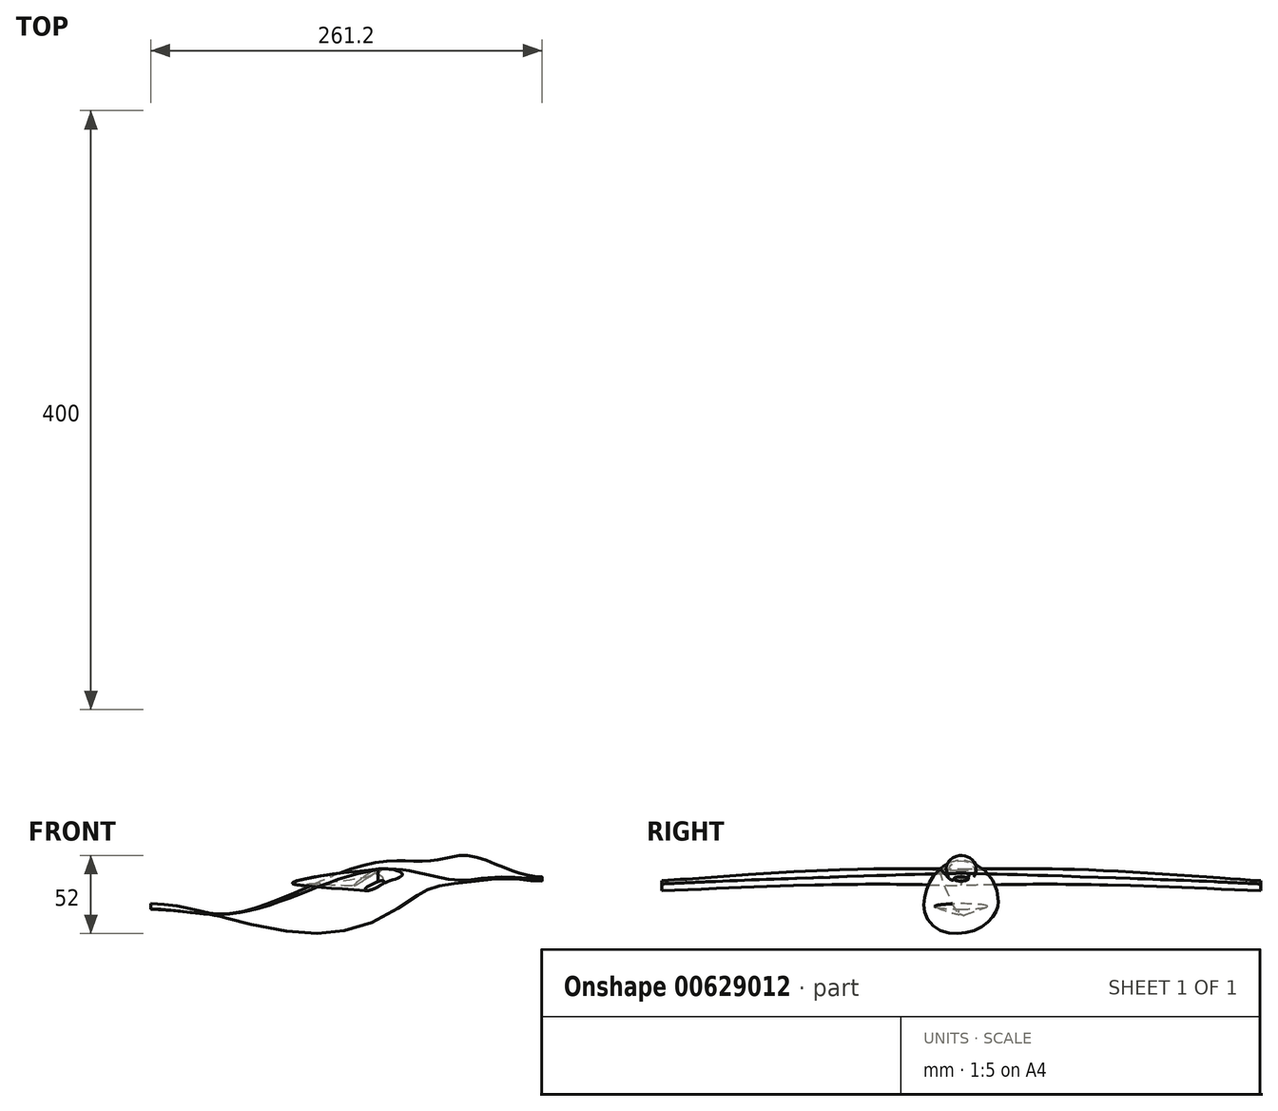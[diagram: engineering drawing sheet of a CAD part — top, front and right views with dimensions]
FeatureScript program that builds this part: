
annotation { "Feature Type Name" : "Feature", "Feature Type Description" : "" }
export const myFeature = defineFeature(function(context is Context, id is Id, definition is map)
    precondition{}
    {
        {
            var Q0;
            Q0=qCreatedBy(makeId("Front.planeOp"),FACE);
            var sketch = newSketch(context, id + "F0", { "sketchPlane" : qUnion([Q0])});
            skFitSpline(sketch, "E0", {"points": [v(-84.41, 5.07) * mm, v(-53.05, 3.5) * mm, v(-25.7, 11.37) * mm, v(6.23, 29.99) * mm, v(29, 38.44) * mm, v(45.9, 41.59) * mm, v(67.8, 40.44) * mm, v(80.55, 33.71) * mm, v(96.01, 29.7) * mm], "startDerivative": vector(310.96, -44.42) * mm, "endDerivative": vector(203.12, -4.15) * mm});
            skSolve(sketch);
        }
        {
            var Q0;
            Q0=qCreatedBy(makeId("Right.planeOp"),FACE);
            cPlane(context, id + "F1", {"entities" : qUnion([Q0]), "cplaneType" : CPlaneType.OFFSET, "offset" : 96 * mm, "width" : 150 * mm, "height" : 150 * mm});
        }
        {
            var Q0;
            Q0=qCreatedBy(makeId("Right.planeOp"),FACE);
            cPlane(context, id + "F2", {"entities" : qUnion([Q0]), "cplaneType" : CPlaneType.OFFSET, "offset" : 116.2 * mm, "oppositeDirection" : true, "width" : 150 * mm, "height" : 150 * mm});
        }
        {
            var Q0;
            Q0=qCreatedBy(id+"F2.planeOp",FACE);
            var sketch = newSketch(context, id + "F3", { "sketchPlane" : qUnion([Q0])});
            skEllipse(sketch, "E1", {"center": v(0, 5.07) * mm, "majorRadius": 2.78 * mm, "minorRadius": 1.24 * mm, "majorAxis": v(1, 0)});
            skSolve(sketch);
        }
        {
            var Q0;
            Q0=qCreatedBy(id+"F1.planeOp",FACE);
            var sketch = newSketch(context, id + "F4", { "sketchPlane" : qUnion([Q0])});
            skEllipse(sketch, "E2", {"center": v(0, 29.7) * mm, "majorRadius": 5 * mm, "minorRadius": 1.42 * mm, "majorAxis": v(-1, 0)});
            skSolve(sketch);
        }
        {
            var Q0;
            Q0=qCreatedBy(makeId("Right.planeOp"),FACE);
            var sketch = newSketch(context, id + "F5", { "sketchPlane" : qUnion([Q0])});
            skEllipse(sketch, "E3", {"center": v(0, 25.98) * mm, "majorRadius": 17.61 * mm, "minorRadius": 16 * mm, "majorAxis": v(-1, 0)});
            skSolve(sketch);
        }
        {
            var Q0;
            Q0=qCreatedBy(makeId("Right.planeOp"),FACE);
            cPlane(context, id + "F6", {"entities" : qUnion([Q0]), "cplaneType" : CPlaneType.OFFSET, "offset" : 45 * mm, "width" : 150 * mm, "height" : 150 * mm});
        }
        {
            var Q0;
            Q0=qCreatedBy(id+"F6.planeOp",FACE);
            var sketch = newSketch(context, id + "F7", { "sketchPlane" : qUnion([Q0])});
            skEllipse(sketch, "E4", {"center": v(0, 36.3) * mm, "majorRadius": 10 * mm, "minorRadius": 9 * mm, "majorAxis": v(-1, 0)});
            skSolve(sketch);
        }
        {
            var Q0;
            Q0=qCreatedBy(id+"F6.planeOp",FACE);
            cPlane(context, id + "F8", {"entities" : qUnion([Q0]), "cplaneType" : CPlaneType.OFFSET, "offset" : 17.1 * mm, "width" : 150 * mm, "height" : 150 * mm});
        }
        {
            var Q0;
            Q0=qCreatedBy(id+"F8.planeOp",FACE);
            var sketch = newSketch(context, id + "F9", { "sketchPlane" : qUnion([Q0])});
            skEllipse(sketch, "E5", {"center": v(0, 35.27) * mm, "majorRadius": 7.9 * mm, "minorRadius": 5.53 * mm, "majorAxis": v(-1, 0)});
            skSolve(sketch);
        }
        {
            var Q0;
            Q0=qCreatedBy(id+"F2.planeOp",FACE);
            cPlane(context, id + "F10", {"entities" : qUnion([Q0]), "cplaneType" : CPlaneType.OFFSET, "offset" : 49 * mm, "oppositeDirection" : true, "width" : 150 * mm, "height" : 150 * mm});
        }
        {
            var Q0;
            Q0=qCreatedBy(id+"F10.planeOp",FACE);
            var sketch = newSketch(context, id + "F11", { "sketchPlane" : qUnion([Q0])});
            skEllipse(sketch, "E6", {"center": v(0, 11.37) * mm, "majorRadius": 17.57 * mm, "minorRadius": 1.8 * mm, "majorAxis": v(-1, 0)});
            skSolve(sketch);
        }
        {
            var Q0;
            Q0=makeQuery(id+"F4.imprint","IMPRINT",FACE,{"disambiguationData":[TD([[makeQuery(id+"F4.imprint","IMPRINT",EDGE,{"derivedFrom":sQuery(id+"F4.wireOp",EDGE,"E2")}),1.0]])]});
            var Q1;
            Q1=makeQuery(id+"F9.imprint","IMPRINT",FACE,{"disambiguationData":[TD([[makeQuery(id+"F9.imprint","IMPRINT",EDGE,{"derivedFrom":sQuery(id+"F9.wireOp",EDGE,"E5")}),1.0]])]});
            var Q2;
            Q2=makeQuery(id+"F7.imprint","IMPRINT",FACE,{"disambiguationData":[TD([[makeQuery(id+"F7.imprint","IMPRINT",EDGE,{"derivedFrom":sQuery(id+"F7.wireOp",EDGE,"E4")}),1.0]])]});
            var Q3;
            Q3=makeQuery(id+"F5.imprint","IMPRINT",FACE,{"disambiguationData":[TD([[makeQuery(id+"F5.imprint","IMPRINT",EDGE,{"derivedFrom":sQuery(id+"F5.wireOp",EDGE,"E3")}),1.0]])]});
            var Q4;
            Q4=makeQuery(id+"F3.imprint","IMPRINT",FACE,{"disambiguationData":[TD([[makeQuery(id+"F3.imprint","IMPRINT",EDGE,{"derivedFrom":sQuery(id+"F3.wireOp",EDGE,"E1")}),1.0]])]});
            var Q5;
            Q5=makeQuery(id+"F11.imprint","IMPRINT",FACE,{"disambiguationData":[TD([[makeQuery(id+"F11.imprint","IMPRINT",EDGE,{"derivedFrom":sQuery(id+"F11.wireOp",EDGE,"E6")}),1.0]])]});
            loft(context, id + "F12", {"startCondition" : LoftEndDerivativeType.NORMAL_TO_PROFILE, "startMagnitude" : 1, "endCondition" : LoftEndDerivativeType.NORMAL_TO_PROFILE, "endMagnitude" : 1, "sheetProfilesArray" : [{ "sheetProfileEntities" : qUnion([Q0]) }, { "sheetProfileEntities" : qUnion([Q1]) }, { "sheetProfileEntities" : qUnion([Q2]) }, { "sheetProfileEntities" : qUnion([Q3]) }, { "sheetProfileEntities" : qUnion([Q4]) }, { "sheetProfileEntities" : qUnion([Q5]) }]});
        }
        {
            var Q0;
            Q0=qCreatedBy(makeId("Front.planeOp"),FACE);
            var sketch = newSketch(context, id + "F13", { "sketchPlane" : qUnion([Q0])});
            skLineSegment(sketch, "E7", {"start": v(-58.76, 13.59) * mm, "end": v(0, 35.7) * mm});
            skSolve(sketch);
        }
        {
            var Q0;
            Q0=qCreatedBy(makeId("Front.planeOp"),FACE);
            cPlane(context, id + "F14", {"entities" : qUnion([Q0]), "cplaneType" : CPlaneType.OFFSET, "offset" : 200 * mm, "width" : 150 * mm, "height" : 150 * mm});
        }
        {
            var Q0;
            Q0=qCreatedBy(makeId("Front.planeOp"),FACE);
            cPlane(context, id + "F15", {"entities" : qUnion([Q0]), "cplaneType" : CPlaneType.OFFSET, "offset" : 49 * mm, "width" : 150 * mm, "height" : 150 * mm});
        }
        {
            var Q0;
            Q0=qCreatedBy(makeId("Front.planeOp"),FACE);
            var sketch = newSketch(context, id + "F16", { "sketchPlane" : qUnion([Q0])});
            skEllipticalArc(sketch, "E8", {});
            skEllipticalArc(sketch, "E9", {});
            const initialGuessF16  = {"E8": [-0.017298103401628084, 0.03379535302519832, -0.8237704339825465, -0.566923515208374, 0.015067684936084414, 0.0010891221126240588, 4.662685079881785, 1.6451477373924313], "E9": [-0.014588911086320877, 0.03496590629220011, 0.9849873090560092, 0.17262676790869394, 0.0029575265624903397, 0.001370500930630289, 4.218962995655077, 2.6759421118494005]};
            skSetInitialGuess(sketch, initialGuessF16);
            skSolve(sketch);
        }
        {
            var Q0;
            Q0=qCreatedBy(id+"F15.planeOp",FACE);
            var sketch = newSketch(context, id + "F17", { "sketchPlane" : qUnion([Q0])});
            skEllipticalArc(sketch, "E10", {});
            skEllipticalArc(sketch, "E11", {});
            const initialGuessF17  = {"E10": [-0.032589975744485855, 0.0313419997692108, -0.9890317433706793, -0.14770311644292416, 0.030822984306227378, 0.0024839906210862156, 4.077982171427082, 2.2809984880084127], "E11": [-0.00894947163760662, 0.03431832045316696, 0.9996639704356599, -0.02592192533005802, 0.008555501838095957, 0.0021409207846646914, 4.29899924266966, 2.3333235677117328]};
            skSetInitialGuess(sketch, initialGuessF17);
            skSolve(sketch);
        }
        {
            var Q0;
            Q0=qCreatedBy(id+"F14.planeOp",FACE);
            var sketch = newSketch(context, id + "F18", { "sketchPlane" : qUnion([Q0])});
            skEllipticalArc(sketch, "E12", {});
            skEllipticalArc(sketch, "E13", {});
            const initialGuessF18  = {"E12": [-0.016077956184744835, 0.024971546605229378, -0.9096880175977404, -0.4152923195040971, 0.0069856411031233275, 0.0016369145110534853, 4.230009728268898, 2.495065859207771], "E13": [-0.01159256137907505, 0.0273281279951334, 0.9853504377429596, 0.1705418272441046, 0.002518639731580008, 0.0011575756907042255, 5.04476189844623, 2.525653687221013]};
            skSetInitialGuess(sketch, initialGuessF18);
            skSolve(sketch);
        }
        {
            var Q0;
            Q0=makeQuery(id+"F16.imprint","IMPRINT",FACE,{"disambiguationData":[TD([[makeQuery(id+"F16.imprint","IMPRINT",EDGE,{"derivedFrom":sQuery(id+"F16.wireOp",EDGE,"E8")}),1.0]])]});
            var Q1;
            Q1=makeQuery(id+"F17.imprint","IMPRINT",FACE,{"disambiguationData":[TD([[makeQuery(id+"F17.imprint","IMPRINT",EDGE,{"derivedFrom":sQuery(id+"F17.wireOp",EDGE,"E10")}),1.0]])]});
            var Q2;
            Q2=makeQuery(id+"F18.imprint","IMPRINT",FACE,{"disambiguationData":[TD([[makeQuery(id+"F18.imprint","IMPRINT",EDGE,{"derivedFrom":sQuery(id+"F18.wireOp",EDGE,"E12")}),1.0]])]});
            loft(context, id + "F19", {"sheetProfilesArray" : [{ "sheetProfileEntities" : qUnion([Q0]) }, { "sheetProfileEntities" : qUnion([Q1]) }, { "sheetProfileEntities" : qUnion([Q2]) }]});
        }
        {
            var Q0;
            Q0=makeQuery(id+"F19.opLoft","SWEPT_BODY",BODY,{"disambiguationData":[OSD([makeQuery(id+"F16.imprint","IMPRINT",FACE,{"disambiguationData":[TD([[makeQuery(id+"F16.imprint","IMPRINT",EDGE,{"derivedFrom":sQuery(id+"F16.wireOp",EDGE,"E8")}),1.0]])]}),sQuery(id+"F17.wireOp",EDGE,"E10"),makeQuery(id+"F18.imprint","IMPRINT",FACE,{"disambiguationData":[TD([[makeQuery(id+"F18.imprint","IMPRINT",EDGE,{"derivedFrom":sQuery(id+"F18.wireOp",EDGE,"E12")}),1.0]])]})])]});
            var Q1;
            Q1=qCreatedBy(makeId("Front.planeOp"),FACE);
            mirror(context, id + "F20", {"entities" : qUnion([Q0]), "mirrorPlane" : qUnion([Q1])});
        }
    });
